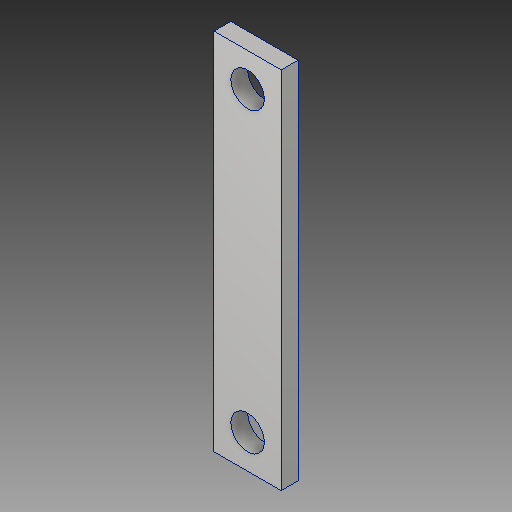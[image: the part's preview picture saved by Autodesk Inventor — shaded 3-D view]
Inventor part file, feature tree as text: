
AUTODESK INVENTOR PART (.ipt)
format: ipt  version: 2018.1 (Build 221171000, 171)  size: 95,744 bytes
history: native  units: mm
features: other x1, extrude x1, sketch x1
ambient origin geometry x8: Origin, YZ Plane, XZ Plane, XY Plane, X Axis, Y Axis, Z Axis, Center Point
bodies: Body1 (feature_tree)
feature tree (3):
  other  "ソリッド1"
  extrude  "押し出し1"  Depth=20.0mm
  sketch  "スケッチ1"
